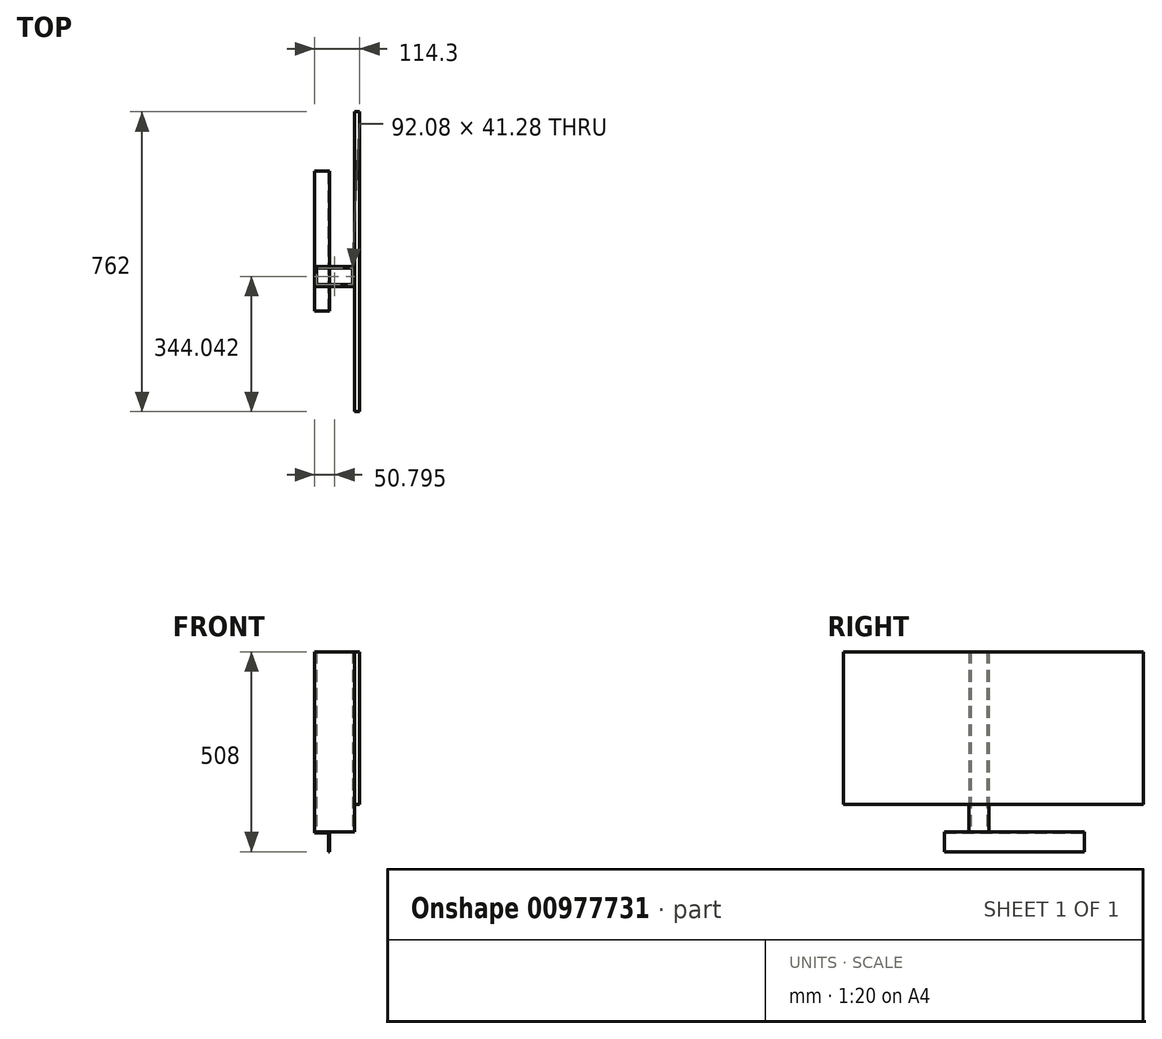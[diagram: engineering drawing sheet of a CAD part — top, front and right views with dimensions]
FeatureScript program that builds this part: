
annotation { "Feature Type Name" : "Feature", "Feature Type Description" : "" }
export const myFeature = defineFeature(function(context is Context, id is Id, definition is map)
    precondition{}
    {
        {
            var Q0;
            Q0=qCreatedBy(makeId("Front.planeOp"),FACE);
            var sketch = newSketch(context, id + "F0", { "sketchPlane" : qUnion([Q0])});
            skLineSegment(sketch, "E0.bottom", {"start": v(-34.93, 27.06) * mm, "end": v(3.17, 27.06) * mm});
            skLineSegment(sketch, "E0.top", {"start": v(-34.93, 23.89) * mm, "end": v(3.17, 23.89) * mm});
            skLineSegment(sketch, "E0.left", {"start": v(-34.93, 27.06) * mm, "end": v(-34.93, 23.89) * mm});
            skLineSegment(sketch, "E0.right", {"start": v(3.17, 27.06) * mm, "end": v(3.17, 23.89) * mm});
            skLineSegment(sketch, "E1.bottom", {"start": v(3.17, 27.06) * mm, "end": v(0, 27.06) * mm});
            skLineSegment(sketch, "E1.top", {"start": v(3.18, -23.74) * mm, "end": v(0, -23.74) * mm});
            skLineSegment(sketch, "E1.left", {"start": v(3.17, 27.06) * mm, "end": v(3.18, -23.74) * mm});
            skLineSegment(sketch, "E1.right", {"start": v(0, 27.06) * mm, "end": v(0, -23.74) * mm});
            skSolve(sketch);
        }
        {
            var Q0;
            Q0 = qSketchRegion(id + "F0", true);
            extrude(context, id + "F1", {"entities" : qUnion([Q0]), "depth" : 355.6 * mm, "offsetDistance" : 25.4 * mm});
        }
        {
            var Q0;
            Q0=makeQuery(id+"F1.opExtrude","SWEPT_FACE",FACE,{"disambiguationData":[OSD([sQuery(id+"F0.wireOp",EDGE,"E0.bottom"),sQuery(id+"F0.wireOp",EDGE,"E1.bottom")])]});
            var sketch = newSketch(context, id + "F2", { "sketchPlane" : qUnion([Q0])});
            skLineSegment(sketch, "E2.bottom", {"start": v(-34.93, -242.08) * mm, "end": v(66.67, -242.08) * mm});
            skLineSegment(sketch, "E2.top", {"start": v(-34.93, -292.88) * mm, "end": v(66.67, -292.88) * mm});
            skLineSegment(sketch, "E2.left", {"start": v(-34.93, -242.08) * mm, "end": v(-34.93, -292.88) * mm});
            skLineSegment(sketch, "E2.right", {"start": v(66.67, -242.08) * mm, "end": v(66.67, -292.88) * mm});
            skLineSegment(sketch, "E3.0", {"start": v(-30.16, -246.84) * mm, "end": v(-30.16, -288.12) * mm});
            skLineSegment(sketch, "E3.1", {"start": v(-30.16, -246.84) * mm, "end": v(61.91, -246.84) * mm});
            skLineSegment(sketch, "E3.2", {"start": v(61.91, -246.84) * mm, "end": v(61.91, -288.12) * mm});
            skLineSegment(sketch, "E3.3", {"start": v(-30.16, -288.12) * mm, "end": v(61.91, -288.12) * mm});
            skSolve(sketch);
        }
        {
            var Q0;
            Q0 = qSketchRegion(id + "F2", true);
            extrude(context, id + "F3", {"entities" : qUnion([Q0]), "depth" : 457.2 * mm, "offsetDistance" : 25.4 * mm});
        }
        {
            var Q0;
            Q0=makeQuery(id+"F3.opExtrude","SWEPT_FACE",FACE,{"disambiguationData":[OSD([sQuery(id+"F2.wireOp",EDGE,"E2.right")])]});
            var sketch = newSketch(context, id + "F4", { "sketchPlane" : qUnion([Q0])});
            skLineSegment(sketch, "E4.bottom", {"start": v(-611.52, 484.26) * mm, "end": v(150.48, 484.26) * mm});
            skLineSegment(sketch, "E4.top", {"start": v(-611.52, 96.91) * mm, "end": v(150.48, 96.91) * mm});
            skLineSegment(sketch, "E4.left", {"start": v(-611.52, 484.26) * mm, "end": v(-611.52, 96.91) * mm});
            skLineSegment(sketch, "E4.right", {"start": v(150.48, 484.26) * mm, "end": v(150.48, 96.91) * mm});
            skSolve(sketch);
        }
        {
            var Q0;
            Q0 = qSketchRegion(id + "F4", true);
            extrude(context, id + "F5", {"entities" : qUnion([Q0]), "depth" : 12.7 * mm, "offsetDistance" : 25.4 * mm});
        }
    });
